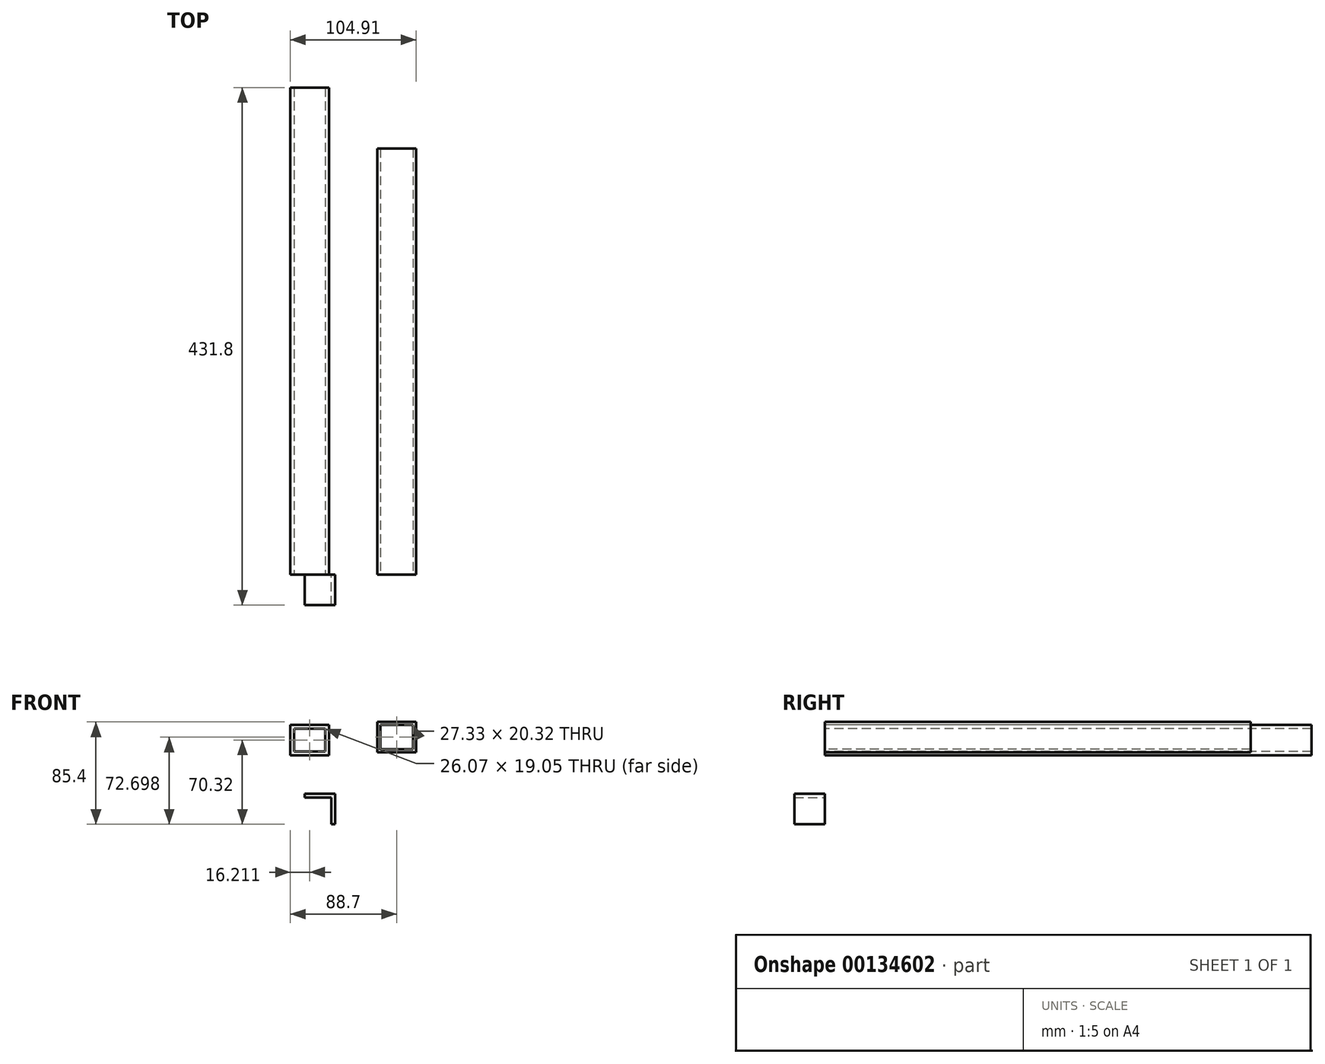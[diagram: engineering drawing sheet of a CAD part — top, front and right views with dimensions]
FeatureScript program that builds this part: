
annotation { "Feature Type Name" : "Feature", "Feature Type Description" : "" }
export const myFeature = defineFeature(function(context is Context, id is Id, definition is map)
    precondition{}
    {
        {
            var Q0;
            Q0=qCreatedBy(makeId("Front.planeOp"),FACE);
            var sketch = newSketch(context, id + "F0", { "sketchPlane" : qUnion([Q0])});
            skLineSegment(sketch, "E0.bottom", {"start": v(-59.75, 30.96) * mm, "end": v(-27.33, 30.96) * mm});
            skLineSegment(sketch, "E0.top", {"start": v(-59.75, 5.56) * mm, "end": v(-27.33, 5.56) * mm});
            skLineSegment(sketch, "E0.left", {"start": v(-59.75, 30.96) * mm, "end": v(-59.75, 5.56) * mm});
            skLineSegment(sketch, "E0.right", {"start": v(-27.33, 30.96) * mm, "end": v(-27.33, 5.56) * mm});
            skPoint(sketch, "E1", {"position": v(-22.47, 51.46) * mm});
            skSolve(sketch);
        }
        {
            var Q0;
            Q0 = qSketchRegion(id + "F0", true);
            extrude(context, id + "F1", {"entities" : qUnion([Q0]), "oppositeDirection" : true, "depth" : 406.4 * mm});
        }
        {
            var Q0;
            Q0=makeQuery(id+"F1.opExtrude","CAP_FACE",FACE,{"disambiguationData":[OSD([sQuery(id+"F0.wireOp",EDGE,"E0.bottom"),sQuery(id+"F0.wireOp",EDGE,"E0.top"),sQuery(id+"F0.wireOp",EDGE,"E0.left"),sQuery(id+"F0.wireOp",EDGE,"E0.right")])],"isStart":true});
            var Q1;
            Q1=makeQuery(id+"F1.opExtrude","CAP_FACE",FACE,{"disambiguationData":[OSD([sQuery(id+"F0.wireOp",EDGE,"E0.bottom"),sQuery(id+"F0.wireOp",EDGE,"E0.top"),sQuery(id+"F0.wireOp",EDGE,"E0.left"),sQuery(id+"F0.wireOp",EDGE,"E0.right")])],"isStart":false});
            shell(context, id + "F2", {"entities" : qUnion([Q0, Q1]), "thickness" : 3.17 * mm});
        }
        {
            var Q0;
            Q0=qCreatedBy(makeId("Front.planeOp"),FACE);
            var sketch = newSketch(context, id + "F3", { "sketchPlane" : qUnion([Q0])});
            skLineSegment(sketch, "E2.bottom", {"start": v(12.74, 33.34) * mm, "end": v(45.16, 33.34) * mm});
            skLineSegment(sketch, "E2.top", {"start": v(12.74, 7.94) * mm, "end": v(45.16, 7.94) * mm});
            skLineSegment(sketch, "E2.left", {"start": v(12.74, 33.34) * mm, "end": v(12.74, 7.94) * mm});
            skLineSegment(sketch, "E2.right", {"start": v(45.16, 33.34) * mm, "end": v(45.16, 7.94) * mm});
            skSolve(sketch);
        }
        {
            var Q0;
            Q0 = qSketchRegion(id + "F3", true);
            extrude(context, id + "F4", {"entities" : qUnion([Q0]), "oppositeDirection" : true, "depth" : 355.6 * mm});
        }
        {
            var Q0;
            Q0=makeQuery(id+"F4.opExtrude","CAP_FACE",FACE,{"disambiguationData":[OSD([sQuery(id+"F3.wireOp",EDGE,"E2.bottom"),sQuery(id+"F3.wireOp",EDGE,"E2.top"),sQuery(id+"F3.wireOp",EDGE,"E2.left"),sQuery(id+"F3.wireOp",EDGE,"E2.right")])],"isStart":true});
            var Q1;
            Q1=makeQuery(id+"F4.opExtrude","CAP_FACE",FACE,{"disambiguationData":[OSD([sQuery(id+"F3.wireOp",EDGE,"E2.bottom"),sQuery(id+"F3.wireOp",EDGE,"E2.top"),sQuery(id+"F3.wireOp",EDGE,"E2.left"),sQuery(id+"F3.wireOp",EDGE,"E2.right")])],"isStart":false});
            shell(context, id + "F5", {"entities" : qUnion([Q0, Q1]), "thickness" : 2.54 * mm});
        }
        {
            var Q0;
            Q0=qCreatedBy(makeId("Front.planeOp"),FACE);
            var sketch = newSketch(context, id + "F6", { "sketchPlane" : qUnion([Q0])});
            skLineSegment(sketch, "E3", {"start": v(-47.95, -26.66) * mm, "end": v(-22.55, -26.66) * mm});
            skLineSegment(sketch, "E4", {"start": v(-22.55, -26.66) * mm, "end": v(-22.55, -52.06) * mm});
            skLineSegment(sketch, "E5", {"start": v(-22.55, -52.06) * mm, "end": v(-25.72, -52.06) * mm});
            skLineSegment(sketch, "E6", {"start": v(-25.72, -52.06) * mm, "end": v(-25.72, -29.83) * mm});
            skLineSegment(sketch, "E7", {"start": v(-25.72, -29.83) * mm, "end": v(-47.95, -29.83) * mm});
            skLineSegment(sketch, "E8", {"start": v(-47.95, -29.83) * mm, "end": v(-47.95, -26.66) * mm});
            skSolve(sketch);
        }
        {
            var Q0;
            Q0=makeQuery(id+"F6.imprint","IMPRINT",FACE,{"disambiguationData":[TD([[makeQuery(id+"F6.imprint","IMPRINT",EDGE,{"derivedFrom":sQuery(id+"F6.wireOp",EDGE,"E3")}),-1.0]])]});
            extrude(context, id + "F7", {"entities" : qUnion([Q0]), "depth" : 25.4 * mm});
        }
    });
